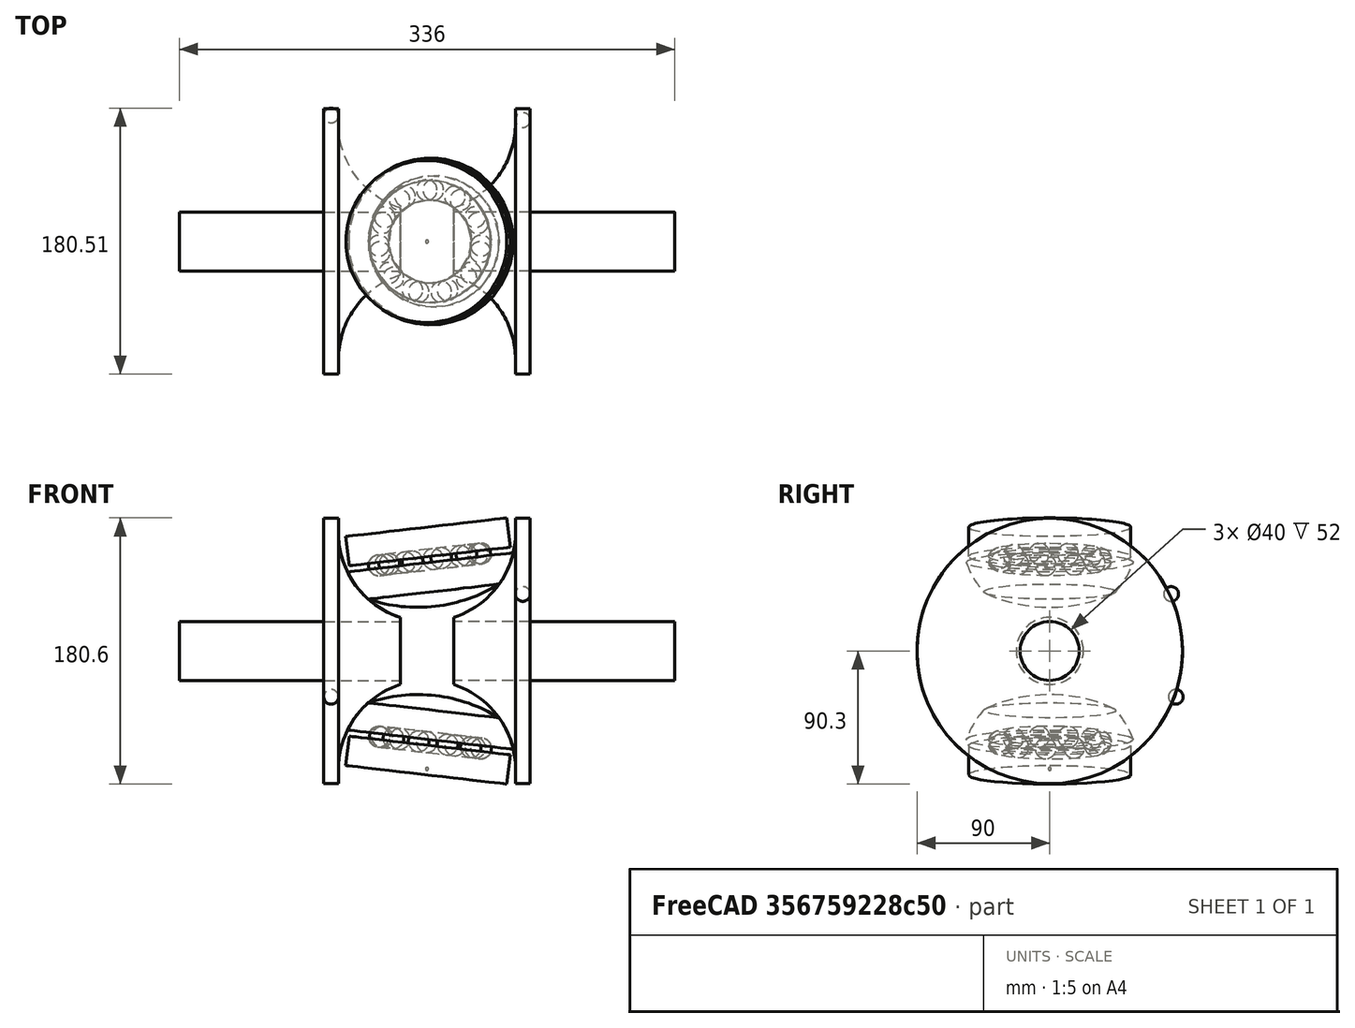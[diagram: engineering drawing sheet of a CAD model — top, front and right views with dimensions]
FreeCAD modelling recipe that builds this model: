
FCSTD DOCUMENT  (FreeCAD 0.18.2R)
Label: TOROIDAL CVT
License: All rights reserved
LicenseURL: http://en.wikipedia.org/wiki/All_rights_reserved
objects: Part::Compound×8, App::DocumentObjectGroupPython×7, Part::Sphere×5, Part::Feature×3, Sketcher::SketchObject×2, PartDesign::Revolution×2, PartDesign::Body×2, Part::Cut×2, Part::Cylinder×2, Part::Torus×1, Part::FeaturePython×1
note: 30 computed .brp shape members not serialized (recipe doc carries the construction recipe); baked Part::Feature solids carry a one-line shape summary decoded from their .brp

FEATURE [Sketcher::SketchObject] Sketch
  MapMode = 5
  Placement = pos=(0,0,0) rot=(1,0,0;1.5708rad)
  Support = -> [XZ_Plane]
  sketch-geometry (4):
    g0: ArcOfCircle CenterX=0 CenterY=0 CenterZ=0 NormalX=0 NormalY=0 NormalZ=1 AngleXU=0 Radius=60 StartAngle=3.48143 EndAngle=3.87132
    g1: ArcOfCircle CenterX=0 CenterY=55 CenterZ=0 NormalX=0 NormalY=0 NormalZ=1 AngleXU=0 Radius=105 StartAngle=4.27241 EndAngle=4.71239
    g2: LineSegment StartX=-56.5685 StartY=-20 StartZ=0 EndX=0 EndY=-20 EndZ=0
    g3: LineSegment StartX=0 StartY=-20 StartZ=0 EndX=0 EndY=-50 EndZ=0
  constraints (13):
    c: Coincident(g0,g-1)
    c: Radius(g0) = 60
    c: DistanceY(g0,g-1) = 20
    c: DistanceY(g0,g-1) = 40
    c: PointOnObject(g1,g-2)
    c: Coincident(g1,g0)
    c: Coincident(g0,g2)
    c: Coincident(g2,g3)
    c: Coincident(g3,g1)
    c: Vertical(g3)
    c: PointOnObject(g2,g-2)
    c: Horizontal(g2)
    c: DistanceY(g1,g-1) = 50
FEATURE [PartDesign::Revolution] Revolution
  Angle = 360
  Axis = (0,0,1)
  Base = (0,0,0)
  Placement = pos=(0,0,0) rot=(1,0,0;1.5708rad)
  Profile = -> Sketch
  ReferenceAxis = -> Sketch [V_Axis]
FEATURE [PartDesign::Body] Body
  Group = -> [Sketch,Revolution]
  Origin = -> Origin
  Tip = -> Revolution
FEATURE [Part::Torus] Torus
  Angle1 = -180
  Angle2 = 180
  Angle3 = 360
  AttacherType = Attacher::AttachEngine3D
  Placement = pos=(0,0,-18) rot=(0,0,1;0rad)
  Radius1 = 35
  Radius2 = 7
FEATURE [Part::Cut] Cut
  Base = -> Body
  Tool = -> Torus
FEATURE [Part::Sphere] Sphere
  Angle1 = -90
  Angle2 = 90
  Angle3 = 360
  AttacherType = Attacher::AttachEngine3D
  Placement = pos=(35,0,-18) rot=(0,0,1;0rad)
  Radius = 7
FEATURE [Part::FeaturePython] Array  # Draft array (typed FeaturePython)
  Angle = 360
  ArrayType = 1
  Axis = (0,0,1)
  Base = -> Sphere
  Center = (0,0,0)
  Fuse = false
  IntervalAxis = (0,0,0)
  IntervalX = (1,0,0)
  IntervalY = (0,1,0)
  IntervalZ = (0,0,0)
  NumberPolar = 11
  NumberX = 2
  NumberY = 2
  NumberZ = 1
FEATURE [Part::Cylinder] Cylinder
  Angle = 360
  AttacherType = Attacher::AttachEngine3D
  Height = 20
  Placement = pos=(0,0,-16) rot=(0,0,1;0rad)
  Radius = 55
FEATURE [Part::Cut] Cut001  label="BASE 1"
  Base = -> Cylinder
  Tool = -> Torus
FEATURE [Sketcher::SketchObject] Sketch001
  MapMode = 5
  Placement = pos=(0,0,0) rot=(1,0,0;1.5708rad)
  Support = -> [XZ_Plane001]
  sketch-geometry (6):
    g0: ArcOfCircle CenterX=0 CenterY=80 CenterZ=0 NormalX=0 NormalY=0 NormalZ=1 AngleXU=0 Radius=60 StartAngle=3.14159 EndAngle=4.4077
    g1: LineSegment StartX=-60 StartY=80 StartZ=0 EndX=-60 EndY=90 EndZ=0
    g2: LineSegment StartX=-60 StartY=90 StartZ=0 EndX=-70 EndY=90 EndZ=0
    g3: LineSegment StartX=-70 StartY=90 StartZ=0 EndX=-70 EndY=20 EndZ=0
    g4: LineSegment StartX=-70 StartY=20 StartZ=0 EndX=-18 EndY=20 EndZ=0
    g5: LineSegment StartX=-18 StartY=20 StartZ=0 EndX=-18 EndY=22.7636 EndZ=0
  constraints (18):
    c: Horizontal(g0,g0)
    c: DistanceX(g0,g0) = 18
    c: Tangent(g0,g1) = 1.5708
    c: Coincident(g1,g2)
    c: Horizontal(g2)
    c: Coincident(g2,g3)
    c: Vertical(g3)
    c: Coincident(g3,g4)
    c: Horizontal(g4)
    c: Coincident(g4,g5)
    c: Coincident(g5,g0)
    c: Vertical(g5)
    c: Equal(g2,g1)
    c: DistanceX(g2,g2) = 10
    c: PointOnObject(g0,g-2)
    c: Radius(g0) = 60
    c: DistanceY(g-1,g0) = 80
    c: DistanceY(g-1,g3) = 20
FEATURE [PartDesign::Revolution] Revolution001
  Angle = 360
  Axis = (1,0,0)
  Base = (0,0,0)
  Placement = pos=(0,0,0) rot=(1,0,0;1.5708rad)
  Profile = -> Sketch001
  ReferenceAxis = -> X_Axis001
FEATURE [PartDesign::Body] Body001
  Group = -> [Sketch001,Revolution001]
  Origin = -> Origin001
  Tip = -> Revolution001
FEATURE [Part::Cylinder] Cylinder001
  Angle = 360
  AttacherType = Attacher::AttachEngine3D
  Height = 150
  Placement = pos=(-18,0,-4e-15) rot=(0,-1,0;1.5708rad)
  Radius = 20
FEATURE [Part::Compound] Compound001
  Links = -> [Revolution001,Cylinder001]
FEATURE [Part::Feature] Compound001001  label="Compound002"
  Placement = pos=(0,0,0) rot=(0,0,1;3.14159rad)
  shape: bbox 150 x 180 x 180 mm, 9 faces, 2 solids (baked)
FEATURE [Part::Sphere] Sphere001
  Angle1 = -90
  Angle2 = 90
  Angle3 = 360
  AttacherType = Attacher::AttachEngine3D
  Placement = pos=(-65,0,91) rot=(0,0,1;0rad)
  Radius = 5
FEATURE [Part::Sphere] Sphere002
  Angle1 = -90
  Angle2 = 90
  Angle3 = 360
  AttacherType = Attacher::AttachEngine3D
  Placement = pos=(65,0,91) rot=(0,0,1;0rad)
  Radius = 5
FEATURE [Part::Compound] Compound001002  label="INPUT SHAFT"
  Links = -> [Compound001,Sphere001]
  Placement = pos=(0,0,0) rot=(1,0,0;4.36332rad)
FEATURE [Part::Compound] Compound001003  label="OUTPUT SHAFT"
  Links = -> [Compound001001,Sphere002]
  Placement = pos=(0,0,0) rot=(1,0,0;5.151rad)
FEATURE [Part::Compound] Compound  label="BEARING 1"
  Links = -> [Array,Cut]
  Placement = pos=(0,0,0) rot=(0,0,1;4.36332rad)
FEATURE [Part::Feature] Cut001001  label="BASE 002"
  Placement = pos=(0,0,0) rot=(0,1,0;3.14159rad)
  shape: bbox 110 x 110 x 22 mm, 5 faces (baked)
FEATURE [Part::Sphere] Sphere003
  Angle1 = -90
  Angle2 = 90
  Angle3 = 360
  AttacherType = Attacher::AttachEngine3D
  Radius = 1
FEATURE [Part::Compound] Compound001004  label="BASE 2"
  Links = -> [Cut001001,Sphere003]
FEATURE [Part::Feature] Compound001005  label="BEARING 002"
  Placement = pos=(0,0,0) rot=(0,0,1;4.36332rad)
  shape: bbox 113.1 x 113.1 x 39 mm, 16 faces, 12 solids (baked)
FEATURE [Part::Sphere] Sphere004
  Angle1 = -90
  Angle2 = 90
  Angle3 = 360
  AttacherType = Attacher::AttachEngine3D
  Radius = 1
FEATURE [Part::Compound] Compound001006  label="BEARING 2"
  Links = -> [Compound001005,Sphere004]
  Placement = pos=(0,0,0) rot=(0,1,0;3.14159rad)
FEATURE [App::DocumentObjectGroupPython] My_Placer  # scripted group (container) (typed FeaturePython)
  Placement = pos=(0,0,0) rot=(1,0,0;10.6465rad)
  RotAxis = (1,0,0)
  RotCenter = (0,0,0)
  arc = time*1000
  arc0 = 0
  arc1 = 90
  target = -> Compound001002
  time = 0.61
  x = 0
  x0 = 0
  x1 = 200
  y = 0
  y0 = 0
  y1 = 0
  z = 0
  z0 = 0
  z1 = 0
FEATURE [App::DocumentObjectGroupPython] My_Placer001  # scripted group (container) (typed FeaturePython)
  Placement = pos=(0,0,0) rot=(0,0,1;10.6465rad)
  RotAxis = (0,0,1)
  RotCenter = (0,0,0)
  arc = time*1000
  arc0 = 0
  arc1 = 90
  target = -> Compound
  time = 0.61
  x = 0
  x0 = 0
  x1 = 200
  y = 0
  y0 = 0
  y1 = 0
  z = 0
  z0 = 0
  z1 = 0
FEATURE [Part::Compound] Compound001007
  Links = -> [Cut001,Compound]
  Placement = pos=(0,0,80) rot=(0,1,0;6.16799rad)
FEATURE [App::DocumentObjectGroupPython] My_Placer002  # scripted group (container) (typed FeaturePython)
  Placement = pos=(0,0,80) rot=(0,1,0;-0.115192rad)
  RotAxis = (0,1,0)
  RotCenter = (0,0,0)
  arc = 30-time*60
  arc0 = 0
  arc1 = 90
  target = -> Compound001007
  time = 0.61
  x = 0
  x0 = 0
  x1 = 200
  y = 0
  y0 = 0
  y1 = 0
  z = 80
  z0 = 0
  z1 = 0
FEATURE [App::DocumentObjectGroupPython] My_Placer003  # scripted group (container) (typed FeaturePython)
  Placement = pos=(0,0,0) rot=(0,0,1;10.6465rad)
  RotAxis = (0,0,1)
  RotCenter = (0,0,0)
  arc = time*1000
  arc0 = 0
  arc1 = 90
  target = -> Compound001005
  time = 0.61
  x = 0
  x0 = 0
  x1 = 200
  y = 0
  y0 = 0
  y1 = 0
  z = 0
  z0 = 0
  z1 = 0
FEATURE [Part::Compound] Compound001008
  Links = -> [Compound001004,Compound001006]
  Placement = pos=(0,0,-80) rot=(0,1,0;0.115192rad)
FEATURE [App::DocumentObjectGroupPython] My_Placer004  # scripted group (container) (typed FeaturePython)
  Placement = pos=(0,0,-80) rot=(0,1,0;0.115192rad)
  RotAxis = (0,1,0)
  RotCenter = (0,0,0)
  arc = -30+time*60
  arc0 = 0
  arc1 = 90
  target = -> Compound001008
  time = 0.61
  x = 0
  x0 = 0
  x1 = 200
  y = 0
  y0 = 0
  y1 = 0
  z = -80
  z0 = 0
  z1 = 0
FEATURE [App::DocumentObjectGroupPython] My_Placer005  # scripted group (container) (typed FeaturePython)
  Placement = pos=(0,0,0) rot=(1,0,0;-13.6986rad)
  RotAxis = (1,0,0)
  RotCenter = (0,0,0)
  arc = -y0
  arc0 = 0
  arc1 = 90
  target = -> Compound001003
  time = 0.61
  x = 0
  x0 = 87.7972
  x1 = 111.862
  y = 0
  y0 = 784.87
  y1 = 0
  z = 0
  z0 = 0
  z1 = 0
  expr: x1 = 160 - 120 * sin(60.641 - time * 60.641)
  expr: y0 = 1000 * x0 / x1
  expr: x0 = 160 - 120 * sin(time * 60.641)
FEATURE [App::DocumentObjectGroupPython] My_Manager  # scripted group (container) (typed FeaturePython)
  Group = -> [My_Placer,My_Placer001,My_Placer002,My_Placer003,My_Placer004,My_Placer005]
  intervall = 100
  sleeptime = 0.02
  start = 0
  step = 62
  text = NO
